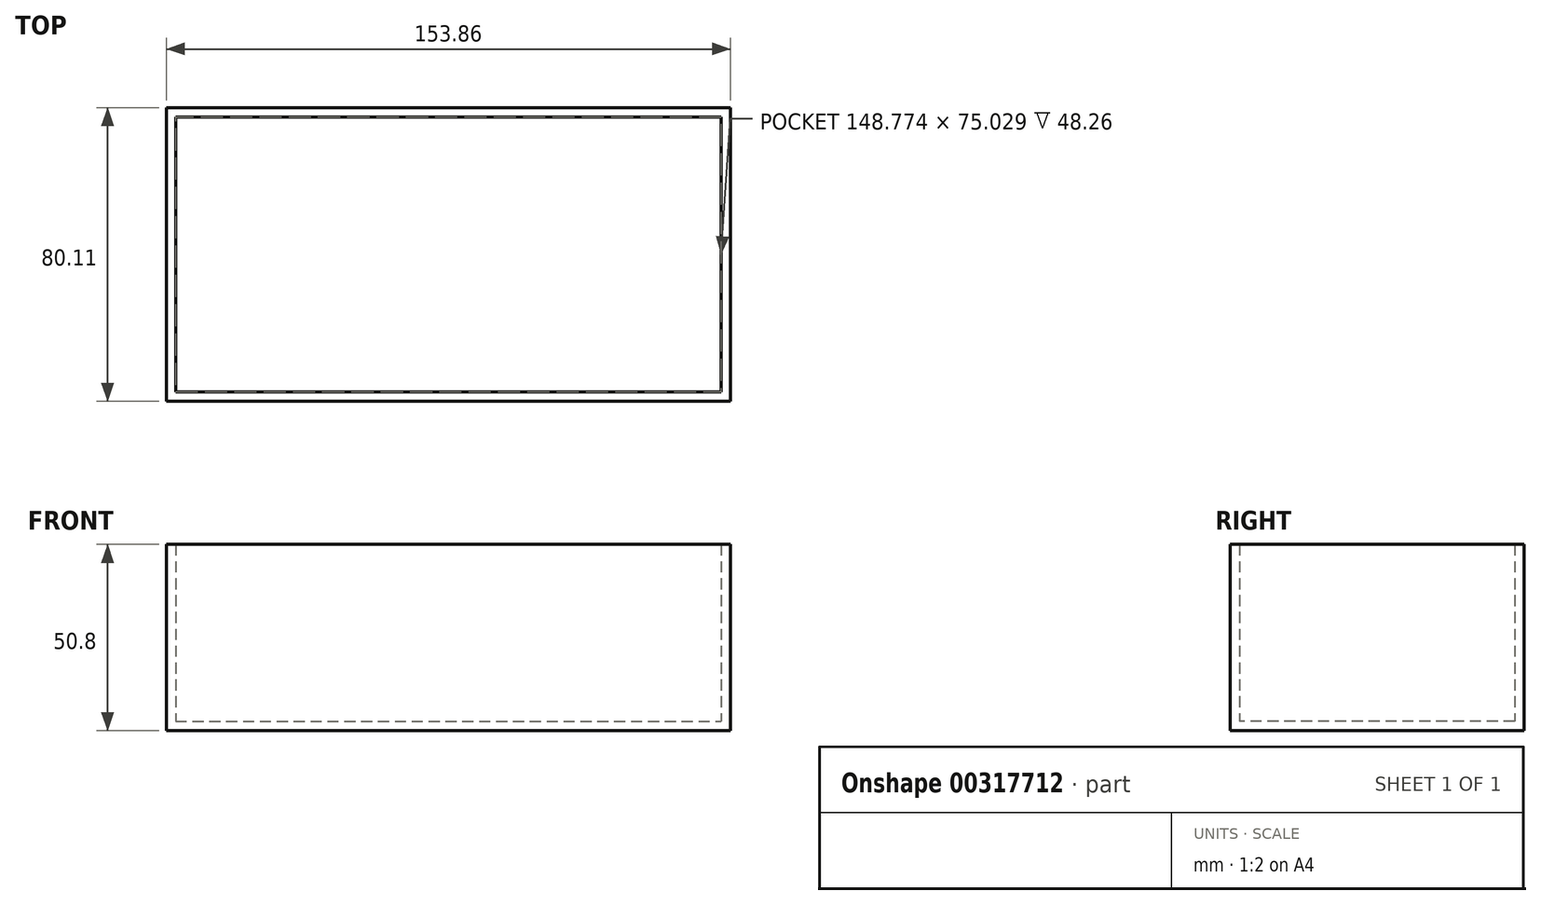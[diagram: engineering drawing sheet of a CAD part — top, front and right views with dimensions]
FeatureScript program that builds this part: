
annotation { "Feature Type Name" : "Feature", "Feature Type Description" : "" }
export const myFeature = defineFeature(function(context is Context, id is Id, definition is map)
    precondition{}
    {
        {
            var Q0;
            Q0=qCreatedBy(makeId("Top.planeOp"),FACE);
            var sketch = newSketch(context, id + "F0", { "sketchPlane" : qUnion([Q0])});
            skLineSegment(sketch, "E0.bottom", {"start": v(-102.92, 55.72) * mm, "end": v(50.94, 55.72) * mm});
            skLineSegment(sketch, "E0.top", {"start": v(-102.92, -24.4) * mm, "end": v(50.94, -24.4) * mm});
            skLineSegment(sketch, "E0.left", {"start": v(-102.92, 55.72) * mm, "end": v(-102.92, -24.4) * mm});
            skLineSegment(sketch, "E0.right", {"start": v(50.94, 55.72) * mm, "end": v(50.94, -24.4) * mm});
            skSolve(sketch);
        }
        {
            var Q0;
            Q0=makeQuery(id+"F0.imprint","IMPRINT",FACE,{"disambiguationData":[TD([[makeQuery(id+"F0.imprint","IMPRINT",EDGE,{"derivedFrom":sQuery(id+"F0.wireOp",EDGE,"E0.bottom")}),-1.0]])]});
            extrude(context, id + "F1", {"entities" : qUnion([Q0]), "depth" : 50.8 * mm});
        }
        {
            var Q0;
            Q0=makeQuery(id+"F1.opExtrude","CAP_FACE",FACE,{"disambiguationData":[OSD([sQuery(id+"F0.wireOp",EDGE,"E0.bottom"),sQuery(id+"F0.wireOp",EDGE,"E0.top"),sQuery(id+"F0.wireOp",EDGE,"E0.left"),sQuery(id+"F0.wireOp",EDGE,"E0.right")])],"isStart":false});
            var sketch = newSketch(context, id + "F2", { "sketchPlane" : qUnion([Q0])});
            skLineSegment(sketch, "E1.bottom", {"start": v(-89.76, -7.39) * mm, "end": v(36.25, -7.39) * mm});
            skLineSegment(sketch, "E1.top", {"start": v(-89.76, 39.74) * mm, "end": v(36.25, 39.74) * mm});
            skLineSegment(sketch, "E1.left", {"start": v(-89.76, -7.39) * mm, "end": v(-89.76, 39.74) * mm});
            skLineSegment(sketch, "E1.right", {"start": v(36.25, -7.39) * mm, "end": v(36.25, 39.74) * mm});
            skSolve(sketch);
        }
        {
            var Q0;
            Q0=makeQuery(id+"F2.imprint","IMPRINT",FACE,{"disambiguationData":[TD([[makeQuery(id+"F2.imprint","IMPRINT",EDGE,{"derivedFrom":sQuery(id+"F2.wireOp",EDGE,"E1.bottom")}),1.0]])]});
            extrude(context, id + "F3", {"entities" : qUnion([Q0]), "operationType" : NewBodyOperationType.ADD, "oppositeDirection" : true, "depth" : 25.4 * mm});
        }
        {
            var Q0;
            Q0 = qSketchRegion(id + "F2", true);
            extrude(context, id + "F4", {"entities" : qUnion([Q0]), "operationType" : NewBodyOperationType.ADD, "oppositeDirection" : true, "depth" : 25.4 * mm});
        }
        {
            var Q0;
            Q0=makeQuery(id+"F1.opExtrude","CAP_FACE",FACE,{"disambiguationData":[OSD([sQuery(id+"F0.wireOp",EDGE,"E0.bottom"),sQuery(id+"F0.wireOp",EDGE,"E0.top"),sQuery(id+"F0.wireOp",EDGE,"E0.left"),sQuery(id+"F0.wireOp",EDGE,"E0.right")])],"isStart":false});
            shell(context, id + "F5", {"entities" : qUnion([Q0]), "thickness" : 2.54 * mm});
        }
    });
